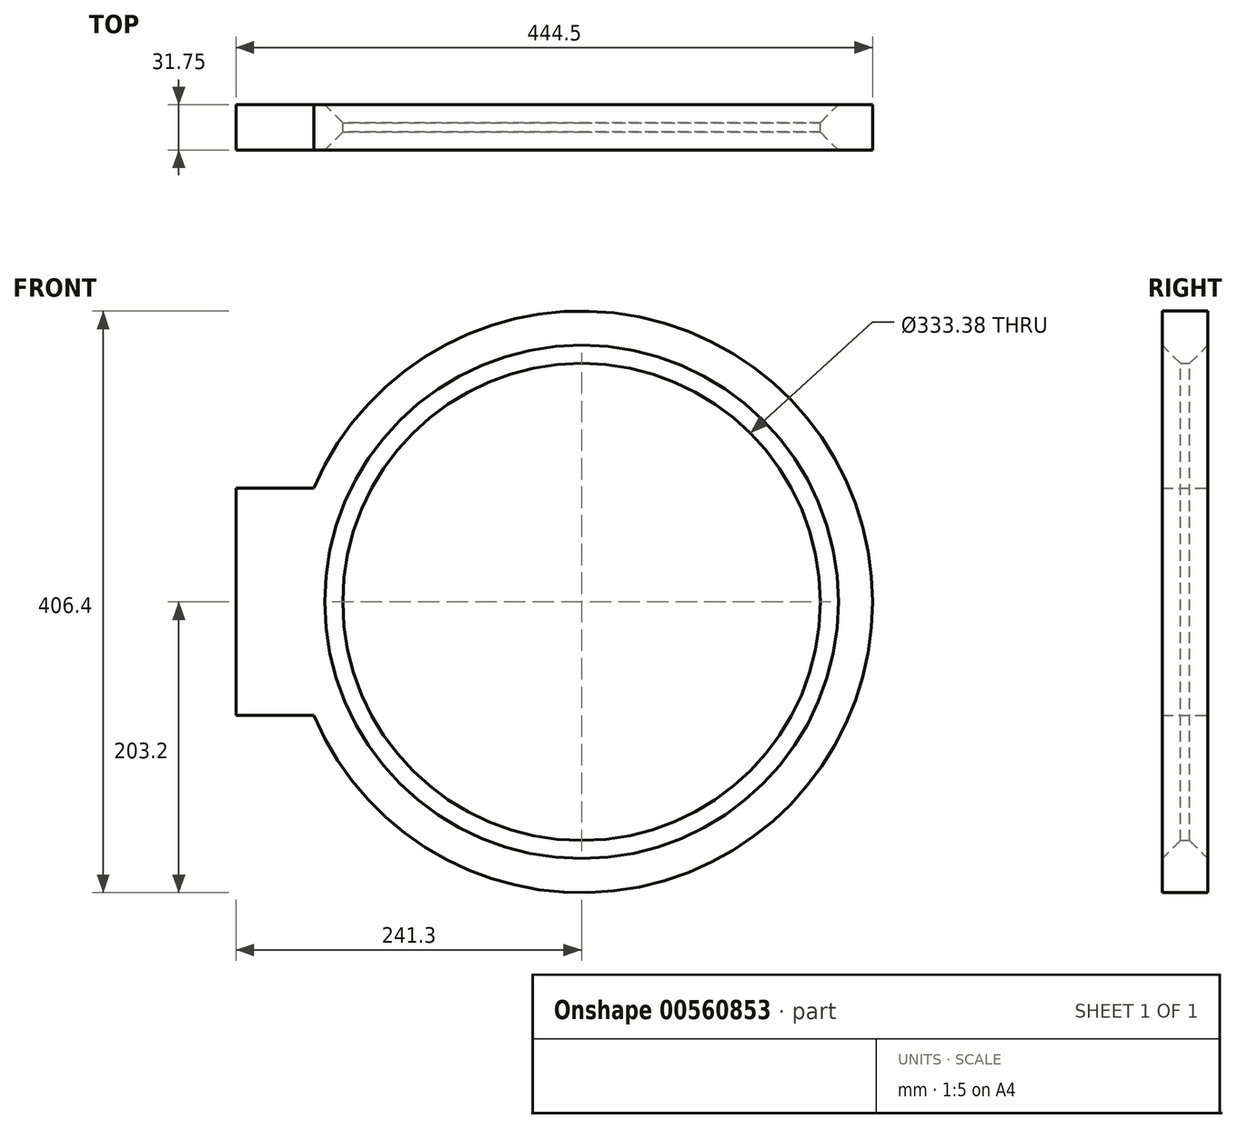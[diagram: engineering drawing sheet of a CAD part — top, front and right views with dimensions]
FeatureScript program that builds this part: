
annotation { "Feature Type Name" : "Feature", "Feature Type Description" : "" }
export const myFeature = defineFeature(function(context is Context, id is Id, definition is map)
    precondition{}
    {
        {
            var Q0;
            Q0=qCreatedBy(makeId("Front.planeOp"),FACE);
            var sketch = newSketch(context, id + "F0", { "sketchPlane" : qUnion([Q0])});
            skCircle(sketch, "E0", {"center": v(0, 0) * mm, "radius": 166.69 * mm});
            skArc(sketch, "E1", {"start": v(-187.06, -79.38) * mm, "mid": v(203.2, 0) * mm, "end": v(-187.06, 79.38) * mm});
            skLineSegment(sketch, "E2", {"start": v(-187.06, 79.38) * mm, "end": v(-241.3, 79.38) * mm});
            skLineSegment(sketch, "E3", {"start": v(-241.3, 79.38) * mm, "end": v(-241.3, -79.38) * mm});
            skLineSegment(sketch, "E4", {"start": v(-241.3, -79.38) * mm, "end": v(-187.06, -79.37) * mm});
            skLineSegment(sketch, "E5", {"start": v(-293.07, 0) * mm, "end": v(0, 0) * mm, "construction": true});
            skSolve(sketch);
        }
        {
            var Q0;
            Q0 = qSketchRegion(id + "F0", true);
            extrude(context, id + "F1", {"entities" : qUnion([Q0]), "depth" : 31.75 * mm, "offsetDistance" : 25.4 * mm});
        }
        {
            var Q0;
            Q0=makeQuery(id+"F1.opExtrude","CAP_EDGE",EDGE,{"disambiguationData":[OSD([sQuery(id+"F0.wireOp",EDGE,"E0")])],"isStart":false});
            var Q1;
            Q1=makeQuery(id+"F1.opExtrude","CAP_EDGE",EDGE,{"disambiguationData":[OSD([sQuery(id+"F0.wireOp",EDGE,"E0")])],"isStart":true});
            chamfer(context, id + "F2", {"entities" : qUnion([Q0, Q1]), "width" : 12.7 * mm, "tangentPropagation" : true});
        }
    });
